# Revit family: Shower_Arm-Rainshower-Grohe-28983_Series
name_source: partatom
category: Plumbing Fixtures
revit_build: Autodesk Revit 2018 (Build: 20170223_1515(x64)
units: mm (PartAtom-declared; Revit-internal decimal feet)

## family parameters
Cut with Voids When Loaded = No
Host = Face
OmniClass Number = 23.45.05.14.17
OmniClass Title = Showers
Part Type = Normal
Room Calculation Point = No
Round Connector Dimension = Use Diameter
Shared = Yes

## types (4) — shared parameters
Assembly Code = D2010700
CW Connection = Yes
CWFU = 3
Cold Water Connection Diameter = 1/2"
Default Elevation = 0"
Description = Wall Mounted 16 Shower Arm
HW Connection = Yes
HWFU = 3
Height = 3 15/16"
Hot Water Connection Diameter = 1/2"
Inlet Connector Diameter = 1/2"
Installation Type = Wall-Mounted
Length = 14 7/8"
Manufacturer = Grohe
Price = Prices may vary. Please consult Manufacturer Representative for most up-to-date price list.
Product Documentation Link = https://americanstandard.box.com
Product Page URL = https://www.grohe.ca
Region = North America
URL = https://www.grohe.ca
Vent Connection = No
WFU = 4
Warranty Information = Lifetime Limited Warranty
Waste Connection = No
Width = 3 3/4"

## per-type parameters (varying)
| type | Body Material | Material |
| 28983000 | Metal-Grohe-000-Starlight Chrome | Metal-Grohe-000-Starlight Chrome |
| 28983EN0 | Metal-Grohe-EN0-Brushed Nickel Infinity Finish | Metal-Grohe-EN0-Brushed Nickel Infinity Finish |
| 28983KS0 | Metal-Grohe-KS0-Velvet Black | Metal-Grohe-KS0-Velvet_Black |
| 28983ZB0 | Metal-Grohe-ZB0-Oiled Rubbed Bronze | Metal-Grohe-ZB0-Oiled Rubbed Bronze |

note: column(s) folded — value = type name in every type: Model

## geometry (parser evidence)
native form markers: Sweep x3
no freeform markers — native parametric forms only
